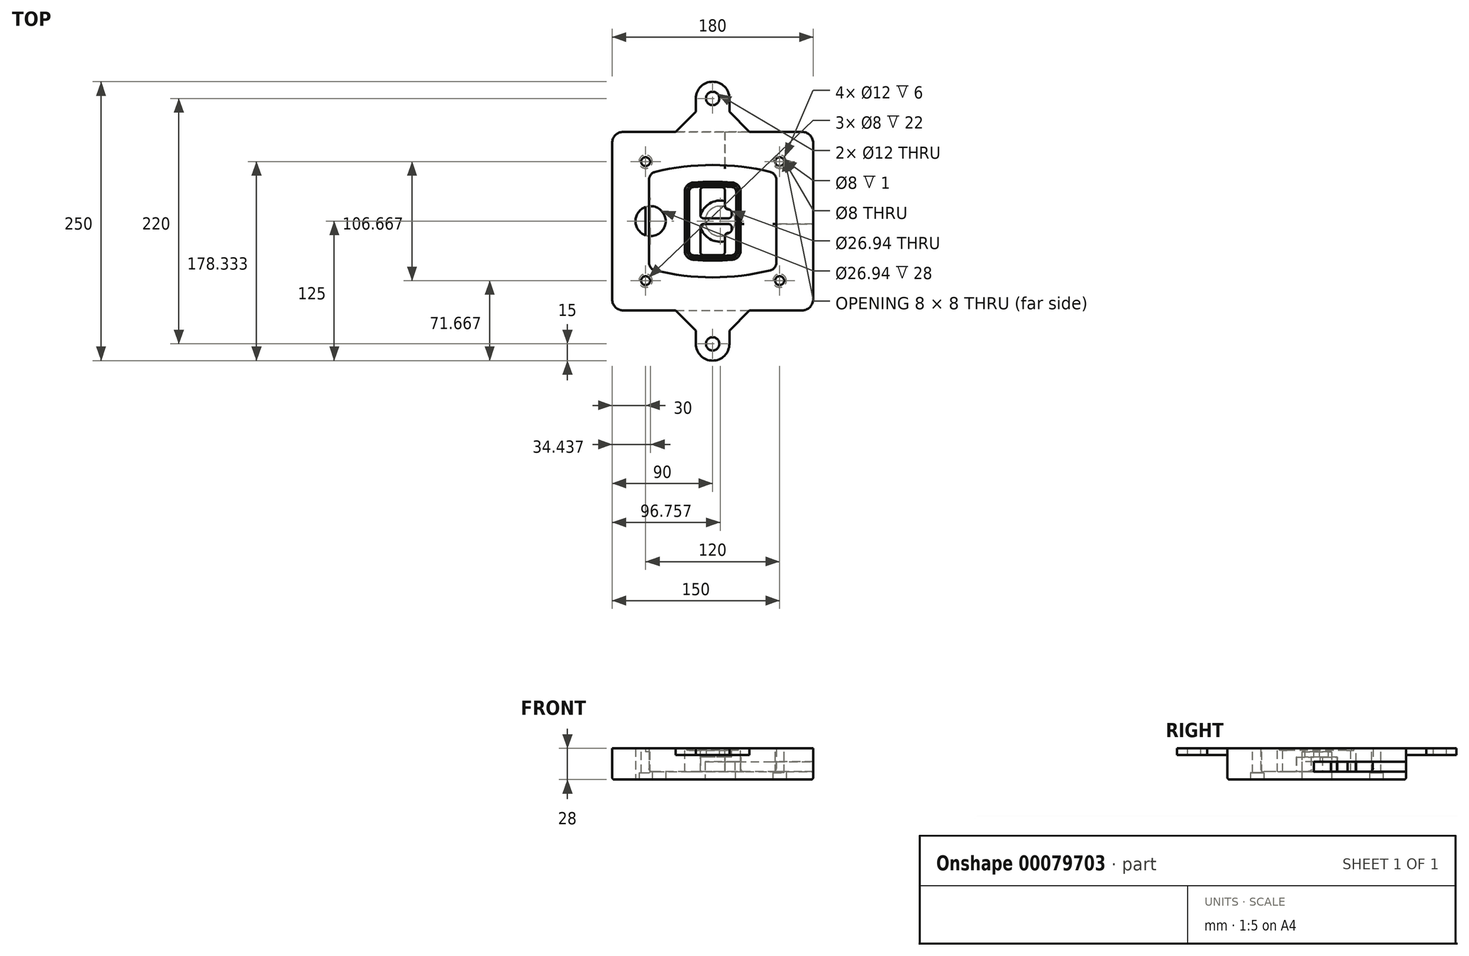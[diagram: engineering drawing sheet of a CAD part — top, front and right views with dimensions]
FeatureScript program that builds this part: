
annotation { "Feature Type Name" : "Feature", "Feature Type Description" : "" }
export const myFeature = defineFeature(function(context is Context, id is Id, definition is map)
    precondition{}
    {
        {
            var Q0;
            Q0=qCreatedBy(makeId("Top.planeOp"),FACE);
            var sketch = newSketch(context, id + "F0", { "sketchPlane" : qUnion([Q0])});
            skPoint(sketch, "E0.rect.middle", {"position": v(0, 0) * mm});
            skLineSegment(sketch, "E1.bottom", {"start": v(-80, -80) * mm, "end": v(80, -80) * mm});
            skLineSegment(sketch, "E1.top", {"start": v(-80, 80) * mm, "end": v(80, 80) * mm});
            skLineSegment(sketch, "E1.left", {"start": v(-90, -70) * mm, "end": v(-90, 70) * mm});
            skLineSegment(sketch, "E1.right", {"start": v(90, -70) * mm, "end": v(90, 70) * mm});
            skLineSegment(sketch, "E2", {"start": v(-90, 80) * mm, "end": v(90, -80) * mm, "construction": true});
            skLineSegment(sketch, "E3", {"start": v(90, 80) * mm, "end": v(-90, -80) * mm, "construction": true});
            skCircle(sketch, "E4", {"center": v(-60, 53.33) * mm, "radius": 4 * mm});
            skCircle(sketch, "E5", {"center": v(60, 53.33) * mm, "radius": 4 * mm});
            skCircle(sketch, "E6", {"center": v(60, -53.33) * mm, "radius": 4 * mm});
            skCircle(sketch, "E7", {"center": v(-60, -53.33) * mm, "radius": 4 * mm});
            skLineSegment(sketch, "E8", {"start": v(-60, 53.33) * mm, "end": v(60, 53.33) * mm, "construction": true});
            skLineSegment(sketch, "E9", {"start": v(60, 53.33) * mm, "end": v(60, -53.33) * mm, "construction": true});
            skLineSegment(sketch, "E10", {"start": v(60, -53.33) * mm, "end": v(-60, -53.33) * mm, "construction": true});
            skLineSegment(sketch, "E11", {"start": v(-60, -53.33) * mm, "end": v(-60, 53.33) * mm, "construction": true});
            skLineSegment(sketch, "E12", {"start": v(-60, 37.3) * mm, "end": v(-60, -37.3) * mm});
            skLineSegment(sketch, "E13", {"start": v(60, 37.3) * mm, "end": v(60, -37.3) * mm});
            skArc(sketch, "E14", {"start": v(52.38, 47.01) * mm, "mid": v(0, 53.33) * mm, "end": v(-52.38, 47.01) * mm});
            skArc(sketch, "E15", {"start": v(-52.38, -47.01) * mm, "mid": v(0, -53.33) * mm, "end": v(52.38, -47.01) * mm});
            skLineSegment(sketch, "E16", {"start": v(-60, 0) * mm, "end": v(60, 0) * mm, "construction": true});
            skPoint(sketch, "E17.visualSharp", {"position": v(-60, -45) * mm});
            skArc(sketch, "E17.filletArc", {"start": v(-60, -37.3) * mm, "mid": v(-57.87, -43.47) * mm, "end": v(-52.38, -47.01) * mm});
            skPoint(sketch, "E18.visualSharp", {"position": v(-60, 45) * mm});
            skArc(sketch, "E18.filletArc", {"start": v(-52.38, 47.01) * mm, "mid": v(-57.87, 43.47) * mm, "end": v(-60, 37.3) * mm});
            skPoint(sketch, "E19.visualSharp", {"position": v(60, 45) * mm});
            skArc(sketch, "E19.filletArc", {"start": v(60, 37.3) * mm, "mid": v(57.87, 43.47) * mm, "end": v(52.38, 47.01) * mm});
            skPoint(sketch, "E20.visualSharp", {"position": v(60, -45) * mm});
            skArc(sketch, "E20.filletArc", {"start": v(52.38, -47.01) * mm, "mid": v(57.87, -43.47) * mm, "end": v(60, -37.3) * mm});
            skPoint(sketch, "E21.visualSharp", {"position": v(-90, 80) * mm});
            skArc(sketch, "E21.filletArc", {"start": v(-80, 80) * mm, "mid": v(-87.07, 77.07) * mm, "end": v(-90, 70) * mm});
            skPoint(sketch, "E22.visualSharp", {"position": v(90, 80) * mm});
            skArc(sketch, "E22.filletArc", {"start": v(90, 70) * mm, "mid": v(87.07, 77.07) * mm, "end": v(80, 80) * mm});
            skPoint(sketch, "E23.visualSharp", {"position": v(90, -80) * mm});
            skArc(sketch, "E23.filletArc", {"start": v(80, -80) * mm, "mid": v(87.07, -77.07) * mm, "end": v(90, -70) * mm});
            skPoint(sketch, "E24.visualSharp", {"position": v(-90, -80) * mm});
            skArc(sketch, "E24.filletArc", {"start": v(-90, -70) * mm, "mid": v(-87.07, -77.07) * mm, "end": v(-80, -80) * mm});
            skArc(sketch, "E25.0", {"start": v(57, 37.3) * mm, "mid": v(55.5, 41.62) * mm, "end": v(51.67, 44.1) * mm});
            skLineSegment(sketch, "E25.1", {"start": v(57, 37.3) * mm, "end": v(57, -37.3) * mm});
            skArc(sketch, "E25.2", {"start": v(51.67, -44.1) * mm, "mid": v(55.5, -41.62) * mm, "end": v(57, -37.3) * mm});
            skArc(sketch, "E25.3", {"start": v(-51.67, -44.1) * mm, "mid": v(0, -50.33) * mm, "end": v(51.67, -44.1) * mm});
            skArc(sketch, "E25.4", {"start": v(-57, -37.3) * mm, "mid": v(-55.5, -41.62) * mm, "end": v(-51.67, -44.1) * mm});
            skArc(sketch, "E25.5", {"start": v(51.67, 44.1) * mm, "mid": v(0, 50.33) * mm, "end": v(-51.67, 44.1) * mm});
            skLineSegment(sketch, "E25.6", {"start": v(-57, 37.3) * mm, "end": v(-57, -37.3) * mm});
            skArc(sketch, "E25.7", {"start": v(-51.67, 44.1) * mm, "mid": v(-55.5, 41.62) * mm, "end": v(-57, 37.3) * mm});
            skArc(sketch, "E26.0", {"start": v(-53.33, 50.9) * mm, "mid": v(-61.01, 45.94) * mm, "end": v(-64, 37.3) * mm});
            skArc(sketch, "E26.1", {"start": v(53.33, 50.9) * mm, "mid": v(0, 57.33) * mm, "end": v(-53.33, 50.9) * mm});
            skArc(sketch, "E26.2", {"start": v(64, 37.3) * mm, "mid": v(61.01, 45.94) * mm, "end": v(53.33, 50.9) * mm});
            skLineSegment(sketch, "E26.3", {"start": v(64, 37.3) * mm, "end": v(64, -37.3) * mm});
            skArc(sketch, "E26.4", {"start": v(53.33, -50.9) * mm, "mid": v(61.01, -45.94) * mm, "end": v(64, -37.3) * mm});
            skLineSegment(sketch, "E26.5", {"start": v(-64, 37.3) * mm, "end": v(-64, -37.3) * mm});
            skArc(sketch, "E26.6", {"start": v(-53.33, -50.9) * mm, "mid": v(0, -57.33) * mm, "end": v(53.33, -50.9) * mm});
            skArc(sketch, "E26.7", {"start": v(-64, -37.3) * mm, "mid": v(-61.01, -45.94) * mm, "end": v(-53.33, -50.9) * mm});
            skSolve(sketch);
        }
        {
            var Q0;
            Q0=makeQuery(id+"F0.imprint","IMPRINT",FACE,{"disambiguationData":[TD([[makeQuery(id+"F0.imprint","IMPRINT",EDGE,{"derivedFrom":sQuery(id+"F0.wireOp",EDGE,"E1.bottom")}),1.0]])]});
            var Q1;
            Q1=makeQuery(id+"F0.imprint","IMPRINT",FACE,{"disambiguationData":[TD([[makeQuery(id+"F0.imprint","IMPRINT",EDGE,{"derivedFrom":sQuery(id+"F0.wireOp",EDGE,"E12")}),1.0]])]});
            var Q2;
            Q2=makeQuery(id+"F0.imprint","IMPRINT",FACE,{"disambiguationData":[TD([[makeQuery(id+"F0.imprint","IMPRINT",EDGE,{"derivedFrom":sQuery(id+"F0.wireOp",EDGE,"E25.0")}),1.0]])]});
            var Q3;
            Q3=makeQuery(id+"F0.imprint","IMPRINT",FACE,{"disambiguationData":[TD([[makeQuery(id+"F0.imprint","IMPRINT",EDGE,{"derivedFrom":sQuery(id+"F0.wireOp",EDGE,"E12")}),-1.0]])]});
            extrude(context, id + "F1", {"entities" : qUnion([Q0, Q1, Q2, Q3]), "oppositeDirection" : true, "depth" : 25 * mm});
        }
        {
            var Q0;
            Q0=makeQuery(id+"F0.imprint","IMPRINT",FACE,{"disambiguationData":[TD([[makeQuery(id+"F0.imprint","IMPRINT",EDGE,{"derivedFrom":sQuery(id+"F0.wireOp",EDGE,"E12")}),1.0]])]});
            extrude(context, id + "F2", {"entities" : qUnion([Q0]), "operationType" : NewBodyOperationType.ADD, "depth" : 3 * mm});
        }
        {
            var Q0;
            Q0=makeQuery(id+"F0.imprint","IMPRINT",FACE,{"disambiguationData":[TD([[makeQuery(id+"F0.imprint","IMPRINT",EDGE,{"derivedFrom":sQuery(id+"F0.wireOp",EDGE,"E25.0")}),1.0]])]});
            extrude(context, id + "F3", {"entities" : qUnion([Q0]), "operationType" : NewBodyOperationType.REMOVE, "oppositeDirection" : true, "depth" : 18 * mm});
        }
        {
            var Q0;
            Q0=makeQuery(id+"F2.opExtrude","CAP_FACE",FACE,{"disambiguationData":[OSD([sQuery(id+"F0.wireOp",EDGE,"E12"),sQuery(id+"F0.wireOp",EDGE,"E13"),sQuery(id+"F0.wireOp",EDGE,"E14"),sQuery(id+"F0.wireOp",EDGE,"E15"),sQuery(id+"F0.wireOp",EDGE,"E17.filletArc"),sQuery(id+"F0.wireOp",EDGE,"E18.filletArc"),sQuery(id+"F0.wireOp",EDGE,"E19.filletArc"),sQuery(id+"F0.wireOp",EDGE,"E20.filletArc"),sQuery(id+"F0.wireOp",EDGE,"E25.0"),sQuery(id+"F0.wireOp",EDGE,"E25.1"),sQuery(id+"F0.wireOp",EDGE,"E25.2"),sQuery(id+"F0.wireOp",EDGE,"E25.3"),sQuery(id+"F0.wireOp",EDGE,"E25.4"),sQuery(id+"F0.wireOp",EDGE,"E25.5"),sQuery(id+"F0.wireOp",EDGE,"E25.6"),sQuery(id+"F0.wireOp",EDGE,"E25.7")])],"isStart":false});
            var sketch = newSketch(context, id + "F4", { "sketchPlane" : qUnion([Q0])});
            skArc(sketch, "E27.0", {"start": v(-17.7, -34.56) * mm, "mid": v(0, -35.33) * mm, "end": v(17.7, -34.56) * mm});
            skArc(sketch, "E28.0", {"start": v(17.7, 34.56) * mm, "mid": v(0, 35.33) * mm, "end": v(-17.7, 34.56) * mm});
            skLineSegment(sketch, "E29", {"start": v(-25, 26.59) * mm, "end": v(-25, -26.59) * mm});
            skLineSegment(sketch, "E30", {"start": v(25, 26.59) * mm, "end": v(25, -26.59) * mm});
            skLineSegment(sketch, "E31", {"start": v(-25, 33.78) * mm, "end": v(25, 33.78) * mm, "construction": true});
            skLineSegment(sketch, "E32", {"start": v(-25, -33.78) * mm, "end": v(25, -33.78) * mm, "construction": true});
            skPoint(sketch, "E33.visualSharp", {"position": v(-25, 33.78) * mm});
            skArc(sketch, "E33.filletArc", {"start": v(-17.7, 34.56) * mm, "mid": v(-22.9, 32) * mm, "end": v(-25, 26.59) * mm});
            skPoint(sketch, "E34.visualSharp", {"position": v(25, 33.78) * mm});
            skArc(sketch, "E34.filletArc", {"start": v(25, 26.59) * mm, "mid": v(22.9, 32) * mm, "end": v(17.7, 34.56) * mm});
            skPoint(sketch, "E35.visualSharp", {"position": v(25, -33.78) * mm});
            skArc(sketch, "E35.filletArc", {"start": v(17.7, -34.56) * mm, "mid": v(22.9, -32) * mm, "end": v(25, -26.59) * mm});
            skPoint(sketch, "E36.visualSharp", {"position": v(-25, -33.78) * mm});
            skArc(sketch, "E36.filletArc", {"start": v(-25, -26.59) * mm, "mid": v(-22.9, -32) * mm, "end": v(-17.7, -34.56) * mm});
            skArc(sketch, "E37.0", {"start": v(51.67, 44.1) * mm, "mid": v(0, 50.33) * mm, "end": v(-51.67, 44.1) * mm});
            skArc(sketch, "E37.1", {"start": v(-51.67, 44.1) * mm, "mid": v(-55.5, 41.62) * mm, "end": v(-57, 37.3) * mm});
            skLineSegment(sketch, "E37.2", {"start": v(-57, 37.3) * mm, "end": v(-57, -37.3) * mm});
            skArc(sketch, "E37.3", {"start": v(-57, -37.3) * mm, "mid": v(-55.5, -41.62) * mm, "end": v(-51.67, -44.1) * mm});
            skArc(sketch, "E37.4", {"start": v(-51.67, -44.1) * mm, "mid": v(0, -50.33) * mm, "end": v(51.67, -44.1) * mm});
            skArc(sketch, "E37.5", {"start": v(51.67, -44.1) * mm, "mid": v(55.5, -41.62) * mm, "end": v(57, -37.3) * mm});
            skLineSegment(sketch, "E37.6", {"start": v(57, 37.3) * mm, "end": v(57, -37.3) * mm});
            skArc(sketch, "E37.7", {"start": v(57, 37.3) * mm, "mid": v(55.5, 41.62) * mm, "end": v(51.67, 44.1) * mm});
            skLineSegment(sketch, "E38.0", {"start": v(23, 26.59) * mm, "end": v(23, -26.59) * mm});
            skArc(sketch, "E38.1", {"start": v(17.53, -32.56) * mm, "mid": v(21.42, -30.64) * mm, "end": v(23, -26.59) * mm});
            skArc(sketch, "E38.2", {"start": v(-17.53, -32.56) * mm, "mid": v(0, -33.33) * mm, "end": v(17.53, -32.56) * mm});
            skArc(sketch, "E38.3", {"start": v(-23, -26.59) * mm, "mid": v(-21.42, -30.64) * mm, "end": v(-17.53, -32.56) * mm});
            skLineSegment(sketch, "E38.4", {"start": v(-23, 26.59) * mm, "end": v(-23, -26.59) * mm});
            skArc(sketch, "E38.5", {"start": v(23, 26.59) * mm, "mid": v(21.42, 30.64) * mm, "end": v(17.53, 32.56) * mm});
            skArc(sketch, "E38.6", {"start": v(-17.53, 32.56) * mm, "mid": v(-21.42, 30.64) * mm, "end": v(-23, 26.59) * mm});
            skArc(sketch, "E38.7", {"start": v(17.53, 32.56) * mm, "mid": v(0, 33.33) * mm, "end": v(-17.53, 32.56) * mm});
            skArc(sketch, "E39.0", {"start": v(21, 26.59) * mm, "mid": v(19.95, 29.29) * mm, "end": v(17.35, 30.57) * mm});
            skLineSegment(sketch, "E39.1", {"start": v(21, 26.59) * mm, "end": v(21, -26.59) * mm});
            skArc(sketch, "E39.2", {"start": v(17.35, -30.57) * mm, "mid": v(19.95, -29.29) * mm, "end": v(21, -26.59) * mm});
            skArc(sketch, "E39.3", {"start": v(-17.35, -30.57) * mm, "mid": v(0, -31.33) * mm, "end": v(17.35, -30.57) * mm});
            skArc(sketch, "E39.4", {"start": v(-21, -26.59) * mm, "mid": v(-19.95, -29.29) * mm, "end": v(-17.35, -30.57) * mm});
            skArc(sketch, "E39.5", {"start": v(17.35, 30.57) * mm, "mid": v(0, 31.33) * mm, "end": v(-17.35, 30.57) * mm});
            skLineSegment(sketch, "E39.6", {"start": v(-21, 26.59) * mm, "end": v(-21, -26.59) * mm});
            skArc(sketch, "E39.7", {"start": v(-17.35, 30.57) * mm, "mid": v(-19.95, 29.29) * mm, "end": v(-21, 26.59) * mm});
            skLineSegment(sketch, "E40", {"start": v(-25, 0) * mm, "end": v(25, 0) * mm, "construction": true});
            skLineSegment(sketch, "E41", {"start": v(-11, 5.5) * mm, "end": v(-11, 27.5) * mm});
            skLineSegment(sketch, "E42", {"start": v(-8, 30.5) * mm, "end": v(8, 30.5) * mm});
            skLineSegment(sketch, "E43", {"start": v(11, 27.5) * mm, "end": v(11, 13.5) * mm});
            skLineSegment(sketch, "E44", {"start": v(14, 10.5) * mm, "end": v(14, 10.5) * mm});
            skLineSegment(sketch, "E45", {"start": v(17, 7.5) * mm, "end": v(17, 5.5) * mm});
            skLineSegment(sketch, "E46", {"start": v(14, 2.5) * mm, "end": v(-8, 2.5) * mm});
            skPoint(sketch, "E47.visualSharp", {"position": v(-11, 30.5) * mm});
            skArc(sketch, "E47.filletArc", {"start": v(-8, 30.5) * mm, "mid": v(-10.12, 29.62) * mm, "end": v(-11, 27.5) * mm});
            skPoint(sketch, "E48.visualSharp", {"position": v(11, 30.5) * mm});
            skArc(sketch, "E48.filletArc", {"start": v(11, 27.5) * mm, "mid": v(10.12, 29.62) * mm, "end": v(8, 30.5) * mm});
            skPoint(sketch, "E49.visualSharp", {"position": v(11, 10.5) * mm});
            skArc(sketch, "E49.filletArc", {"start": v(11, 13.5) * mm, "mid": v(11.88, 11.38) * mm, "end": v(14, 10.5) * mm});
            skPoint(sketch, "E50.visualSharp", {"position": v(17, 10.5) * mm});
            skArc(sketch, "E50.filletArc", {"start": v(17, 7.5) * mm, "mid": v(16.12, 9.62) * mm, "end": v(14, 10.5) * mm});
            skPoint(sketch, "E51.visualSharp", {"position": v(17, 2.5) * mm});
            skArc(sketch, "E51.filletArc", {"start": v(14, 2.5) * mm, "mid": v(16.12, 3.38) * mm, "end": v(17, 5.5) * mm});
            skPoint(sketch, "E52.visualSharp", {"position": v(-11, 2.5) * mm});
            skArc(sketch, "E52.filletArc", {"start": v(-11, 5.5) * mm, "mid": v(-10.12, 3.38) * mm, "end": v(-8, 2.5) * mm});
            skLineSegment(sketch, "E53.0.MirrorCS", {"start": v(14, -2.5) * mm, "end": v(-8, -2.5) * mm});
            skArc(sketch, "E54.0.MirrorCS", {"start": v(-11, -5.5) * mm, "mid": v(-10.12, -3.38) * mm, "end": v(-8, -2.5) * mm});
            skLineSegment(sketch, "E55.0.MirrorCS", {"start": v(-11, -5.5) * mm, "end": v(-11, -27.5) * mm});
            skArc(sketch, "E56.0.MirrorCS", {"start": v(-8, -30.5) * mm, "mid": v(-10.12, -29.62) * mm, "end": v(-11, -27.5) * mm});
            skLineSegment(sketch, "E57.0.MirrorCS", {"start": v(-8, -30.5) * mm, "end": v(8, -30.5) * mm});
            skArc(sketch, "E58.0.MirrorCS", {"start": v(11, -27.5) * mm, "mid": v(10.12, -29.62) * mm, "end": v(8, -30.5) * mm});
            skLineSegment(sketch, "E59.0.MirrorCS", {"start": v(11, -27.5) * mm, "end": v(11, -13.5) * mm});
            skArc(sketch, "E60.0.MirrorCS", {"start": v(11, -13.5) * mm, "mid": v(11.88, -11.38) * mm, "end": v(14, -10.5) * mm});
            skArc(sketch, "E61.0.MirrorCS", {"start": v(17, -7.5) * mm, "mid": v(16.12, -9.62) * mm, "end": v(14, -10.5) * mm});
            skLineSegment(sketch, "E62.0.MirrorCS", {"start": v(17, -7.5) * mm, "end": v(17, -5.5) * mm});
            skArc(sketch, "E63.0.MirrorCS", {"start": v(14, -2.5) * mm, "mid": v(16.12, -3.38) * mm, "end": v(17, -5.5) * mm});
            skSolve(sketch);
        }
        {
            var Q0;
            Q0=makeQuery(id+"F4.imprint","IMPRINT",FACE,{"disambiguationData":[TD([[makeQuery(id+"F4.imprint","IMPRINT",EDGE,{"derivedFrom":sQuery(id+"F4.wireOp",EDGE,"E27.0")}),1.0]])]});
            var Q1;
            Q1=makeQuery(id+"F4.imprint","IMPRINT",FACE,{"disambiguationData":[TD([[makeQuery(id+"F4.imprint","IMPRINT",EDGE,{"derivedFrom":sQuery(id+"F4.wireOp",EDGE,"E38.0")}),-1.0]])]});
            var Q2;
            Q2=makeQuery(id+"F4.imprint","IMPRINT",FACE,{"disambiguationData":[TD([[makeQuery(id+"F4.imprint","IMPRINT",EDGE,{"derivedFrom":sQuery(id+"F4.wireOp",EDGE,"E39.0")}),1.0]])]});
            extrude(context, id + "F5", {"entities" : qUnion([Q0, Q1, Q2]), "operationType" : NewBodyOperationType.ADD, "endBound" : BoundingType.UP_TO_NEXT, "oppositeDirection" : true, "depth" : 25 * mm});
        }
        {
            var Q0;
            Q0=makeQuery(id+"F4.imprint","IMPRINT",FACE,{"disambiguationData":[TD([[makeQuery(id+"F4.imprint","IMPRINT",EDGE,{"derivedFrom":sQuery(id+"F4.wireOp",EDGE,"E38.0")}),-1.0]])]});
            extrude(context, id + "F6", {"entities" : qUnion([Q0]), "operationType" : NewBodyOperationType.REMOVE, "oppositeDirection" : true, "depth" : 2 * mm});
        }
        {
            var Q0;
            Q0=makeQuery(id+"F1.opExtrude","CAP_FACE",FACE,{"disambiguationData":[OSD([sQuery(id+"F0.wireOp",EDGE,"E1.bottom"),sQuery(id+"F0.wireOp",EDGE,"E1.top"),sQuery(id+"F0.wireOp",EDGE,"E1.left"),sQuery(id+"F0.wireOp",EDGE,"E1.right"),sQuery(id+"F0.wireOp",EDGE,"E4"),sQuery(id+"F0.wireOp",EDGE,"E5"),sQuery(id+"F0.wireOp",EDGE,"E6"),sQuery(id+"F0.wireOp",EDGE,"E7"),sQuery(id+"F0.wireOp",EDGE,"E21.filletArc"),sQuery(id+"F0.wireOp",EDGE,"E22.filletArc"),sQuery(id+"F0.wireOp",EDGE,"E23.filletArc"),sQuery(id+"F0.wireOp",EDGE,"E24.filletArc")])],"isStart":false});
            var sketch = newSketch(context, id + "F7", { "sketchPlane" : qUnion([Q0])});
            skCircle(sketch, "E64", {"center": v(6.76, 0) * mm, "radius": 13.47 * mm});
            skCircle(sketch, "E65", {"center": v(-55.56, 0) * mm, "radius": 13.47 * mm});
            skLineSegment(sketch, "E66", {"start": v(90, 0) * mm, "end": v(-90, 0) * mm});
            skCircle(sketch, "E67", {"center": v(6.76, 0) * mm, "radius": 18.47 * mm});
            skCircle(sketch, "E68", {"center": v(60, -53.33) * mm, "radius": 6 * mm});
            skCircle(sketch, "E69", {"center": v(-60, -53.33) * mm, "radius": 6 * mm});
            skCircle(sketch, "E70", {"center": v(-60, 53.33) * mm, "radius": 6 * mm});
            skCircle(sketch, "E71", {"center": v(60, 53.33) * mm, "radius": 6 * mm});
            skSolve(sketch);
        }
        {
            var Q0;
            {var subQ1=sQuery(id+"F7.wireOp",EDGE,"E66");var subQ4=sQuery(id+"F7.wireOp",EDGE,"E64");var subQ6=makeQuery(id+"F7.imprint","INTERSECT",VERTEX,{"disambiguationData":[OD(0.0)],"derivedFrom":[subQ4,subQ1]});Q0=makeQuery(id+"F7.imprint","IMPRINT",FACE,{"disambiguationData":[TD([[makeQuery(id+"F7.imprint","IMPRINT",EDGE,{"disambiguationData":[TD([[subQ6,-1.0]])],"derivedFrom":subQ4}),-1.0]])]});}
            var Q1;
            {var subQ0=sQuery(id+"F7.wireOp",EDGE,"E66");var subQ1=sQuery(id+"F7.wireOp",EDGE,"E64");var subQ3=makeQuery(id+"F7.imprint","INTERSECT",VERTEX,{"disambiguationData":[OD(0.0)],"derivedFrom":[subQ1,subQ0]});Q1=makeQuery(id+"F7.imprint","IMPRINT",FACE,{"disambiguationData":[TD([[makeQuery(id+"F7.imprint","IMPRINT",EDGE,{"disambiguationData":[TD([[subQ3,-1.0]])],"derivedFrom":subQ1}),1.0]])]});}
            var Q2;
            {var subQ0=sQuery(id+"F7.wireOp",EDGE,"E66");var subQ1=sQuery(id+"F7.wireOp",EDGE,"E64");var subQ3=makeQuery(id+"F7.imprint","INTERSECT",VERTEX,{"disambiguationData":[OD(0.0)],"derivedFrom":[subQ1,subQ0]});Q2=makeQuery(id+"F7.imprint","IMPRINT",FACE,{"disambiguationData":[TD([[makeQuery(id+"F7.imprint","IMPRINT",EDGE,{"disambiguationData":[TD([[subQ3,1.0]])],"derivedFrom":subQ1}),1.0]])]});}
            var Q3;
            {var subQ1=sQuery(id+"F7.wireOp",EDGE,"E66");var subQ4=sQuery(id+"F7.wireOp",EDGE,"E64");var subQ6=makeQuery(id+"F7.imprint","INTERSECT",VERTEX,{"disambiguationData":[OD(0.0)],"derivedFrom":[subQ4,subQ1]});Q3=makeQuery(id+"F7.imprint","IMPRINT",FACE,{"disambiguationData":[TD([[makeQuery(id+"F7.imprint","IMPRINT",EDGE,{"disambiguationData":[TD([[subQ6,1.0]])],"derivedFrom":subQ4}),-1.0]])]});}
            extrude(context, id + "F8", {"entities" : qUnion([Q0, Q1, Q2, Q3]), "operationType" : NewBodyOperationType.ADD, "oppositeDirection" : true, "depth" : 20 * mm});
        }
        {
            var Q0;
            {var subQ0=sQuery(id+"F7.wireOp",EDGE,"E66");var subQ1=sQuery(id+"F7.wireOp",EDGE,"E64");var subQ3=makeQuery(id+"F7.imprint","INTERSECT",VERTEX,{"disambiguationData":[OD(0.0)],"derivedFrom":[subQ1,subQ0]});Q0=makeQuery(id+"F7.imprint","IMPRINT",FACE,{"disambiguationData":[TD([[makeQuery(id+"F7.imprint","IMPRINT",EDGE,{"disambiguationData":[TD([[subQ3,-1.0]])],"derivedFrom":subQ1}),1.0]])]});}
            var Q1;
            {var subQ0=sQuery(id+"F7.wireOp",EDGE,"E66");var subQ1=sQuery(id+"F7.wireOp",EDGE,"E64");var subQ3=makeQuery(id+"F7.imprint","INTERSECT",VERTEX,{"disambiguationData":[OD(0.0)],"derivedFrom":[subQ1,subQ0]});Q1=makeQuery(id+"F7.imprint","IMPRINT",FACE,{"disambiguationData":[TD([[makeQuery(id+"F7.imprint","IMPRINT",EDGE,{"disambiguationData":[TD([[subQ3,1.0]])],"derivedFrom":subQ1}),1.0]])]});}
            extrude(context, id + "F9", {"entities" : qUnion([Q0, Q1]), "operationType" : NewBodyOperationType.REMOVE, "oppositeDirection" : true, "depth" : 16 * mm});
        }
        {
            var Q0;
            {var subQ0=sQuery(id+"F7.wireOp",EDGE,"E66");var subQ1=sQuery(id+"F7.wireOp",EDGE,"E65");var subQ3=makeQuery(id+"F7.imprint","INTERSECT",VERTEX,{"disambiguationData":[OD(0.0)],"derivedFrom":[subQ1,subQ0]});Q0=makeQuery(id+"F7.imprint","IMPRINT",FACE,{"disambiguationData":[TD([[makeQuery(id+"F7.imprint","IMPRINT",EDGE,{"disambiguationData":[TD([[subQ3,-1.0]])],"derivedFrom":subQ1}),1.0]])]});}
            var Q1;
            {var subQ0=sQuery(id+"F7.wireOp",EDGE,"E66");var subQ1=sQuery(id+"F7.wireOp",EDGE,"E65");var subQ3=makeQuery(id+"F7.imprint","INTERSECT",VERTEX,{"disambiguationData":[OD(0.0)],"derivedFrom":[subQ1,subQ0]});Q1=makeQuery(id+"F7.imprint","IMPRINT",FACE,{"disambiguationData":[TD([[makeQuery(id+"F7.imprint","IMPRINT",EDGE,{"disambiguationData":[TD([[subQ3,1.0]])],"derivedFrom":subQ1}),1.0]])]});}
            extrude(context, id + "F10", {"entities" : qUnion([Q0, Q1]), "operationType" : NewBodyOperationType.REMOVE, "oppositeDirection" : true, "depth" : 25 * mm});
        }
        {
            var Q0;
            Q0=makeQuery(id+"F7.imprint","IMPRINT",FACE,{"disambiguationData":[TD([[makeQuery(id+"F7.imprint","IMPRINT",EDGE,{"derivedFrom":sQuery(id+"F7.wireOp",EDGE,"E68")}),1.0]])]});
            var Q1;
            Q1=makeQuery(id+"F7.imprint","IMPRINT",FACE,{"disambiguationData":[TD([[makeQuery(id+"F7.imprint","IMPRINT",EDGE,{"derivedFrom":makeQuery(id+"F1.opExtrude","CAP_EDGE",EDGE,{"disambiguationData":[OSD([sQuery(id+"F0.wireOp",EDGE,"E5")])],"isStart":false})}),-1.0]])]});
            var Q2;
            Q2=makeQuery(id+"F7.imprint","IMPRINT",FACE,{"disambiguationData":[TD([[makeQuery(id+"F7.imprint","IMPRINT",EDGE,{"derivedFrom":sQuery(id+"F7.wireOp",EDGE,"E69")}),1.0]])]});
            var Q3;
            Q3=makeQuery(id+"F7.imprint","IMPRINT",FACE,{"disambiguationData":[TD([[makeQuery(id+"F7.imprint","IMPRINT",EDGE,{"derivedFrom":makeQuery(id+"F1.opExtrude","CAP_EDGE",EDGE,{"disambiguationData":[OSD([sQuery(id+"F0.wireOp",EDGE,"E4")])],"isStart":false})}),-1.0]])]});
            var Q4;
            Q4=makeQuery(id+"F7.imprint","IMPRINT",FACE,{"disambiguationData":[TD([[makeQuery(id+"F7.imprint","IMPRINT",EDGE,{"derivedFrom":sQuery(id+"F7.wireOp",EDGE,"E70")}),1.0]])]});
            var Q5;
            Q5=makeQuery(id+"F7.imprint","IMPRINT",FACE,{"disambiguationData":[TD([[makeQuery(id+"F7.imprint","IMPRINT",EDGE,{"derivedFrom":makeQuery(id+"F1.opExtrude","CAP_EDGE",EDGE,{"disambiguationData":[OSD([sQuery(id+"F0.wireOp",EDGE,"E7")])],"isStart":false})}),-1.0]])]});
            var Q6;
            Q6=makeQuery(id+"F7.imprint","IMPRINT",FACE,{"disambiguationData":[TD([[makeQuery(id+"F7.imprint","IMPRINT",EDGE,{"derivedFrom":sQuery(id+"F7.wireOp",EDGE,"E71")}),1.0]])]});
            var Q7;
            Q7=makeQuery(id+"F7.imprint","IMPRINT",FACE,{"disambiguationData":[TD([[makeQuery(id+"F7.imprint","IMPRINT",EDGE,{"derivedFrom":makeQuery(id+"F1.opExtrude","CAP_EDGE",EDGE,{"disambiguationData":[OSD([sQuery(id+"F0.wireOp",EDGE,"E6")])],"isStart":false})}),-1.0]])]});
            extrude(context, id + "F11", {"entities" : qUnion([Q0, Q1, Q2, Q3, Q4, Q5, Q6, Q7]), "operationType" : NewBodyOperationType.REMOVE, "oppositeDirection" : true, "depth" : 6 * mm});
        }
        {
            var Q0;
            Q0=makeQuery(id+"F9.boolean.opBoolean","COPY",FACE,{"derivedFrom":makeQuery(id+"F9.opExtrude","CAP_FACE",FACE,{"disambiguationData":[OSD([sQuery(id+"F7.wireOp",EDGE,"E64")])],"isStart":false})});
            var sketch = newSketch(context, id + "F12", { "sketchPlane" : qUnion([Q0])});
            skArc(sketch, "E72.0", {"start": v(11, -88.19) * mm, "mid": v(97.1, -83.6) * mm, "end": v(92.5, 2.5) * mm});
            skLineSegment(sketch, "E72.1", {"start": v(11, -17.97) * mm, "end": v(11, -17.97) * mm});
            skLineSegment(sketch, "E73", {"start": v(92.5, -105.13) * mm, "end": v(102.3, -105.13) * mm});
            skLineSegment(sketch, "E74.0", {"start": v(92.5, 2.5) * mm, "end": v(14, 2.5) * mm});
            skArc(sketch, "E74.1", {"start": v(14, 2.5) * mm, "mid": v(16.12, 3.38) * mm, "end": v(17, 5.5) * mm});
            skLineSegment(sketch, "E74.2", {"start": v(17, 7.5) * mm, "end": v(17, 5.5) * mm});
            skArc(sketch, "E74.3", {"start": v(17, 7.5) * mm, "mid": v(16.12, 9.62) * mm, "end": v(14, 10.5) * mm});
            skArc(sketch, "E74.4", {"start": v(11, 13.5) * mm, "mid": v(11.88, 11.38) * mm, "end": v(14, 10.5) * mm});
            skLineSegment(sketch, "E74.5", {"start": v(11, 13.5) * mm, "end": v(11, -88.19) * mm});
            skLineSegment(sketch, "E74.7", {"start": v(92.5, -2.5) * mm, "end": v(14, -2.5) * mm});
            skArc(sketch, "E74.8", {"start": v(14, -2.5) * mm, "mid": v(16.12, -3.38) * mm, "end": v(17, -5.5) * mm});
            skLineSegment(sketch, "E74.9", {"start": v(17, -7.5) * mm, "end": v(17, -5.5) * mm});
            skArc(sketch, "E74.10", {"start": v(17, -7.5) * mm, "mid": v(16.12, -9.62) * mm, "end": v(14, -10.5) * mm});
            skArc(sketch, "E74.11", {"start": v(11, -13.5) * mm, "mid": v(11.88, -11.38) * mm, "end": v(14, -10.5) * mm});
            skLineSegment(sketch, "E74.12", {"start": v(11, -17.97) * mm, "end": v(11, -13.5) * mm});
            skPoint(sketch, "E75.orphan", {"position": v(11, -27.5) * mm});
            skPoint(sketch, "E76.orphan", {"position": v(-8, -2.5) * mm});
            skPoint(sketch, "E77.orphan", {"position": v(-8, 2.5) * mm});
            skPoint(sketch, "E78.orphan", {"position": v(11, 27.5) * mm});
            skSolve(sketch);
        }
        {
            var Q0;
            {var subQ7=sQuery(id+"F12.wireOp",EDGE,"E72.0");var subQ14=sQuery(id+"F12.wireOp",EDGE,"E72.1");var subQ16=sQuery(id+"F12.wireOp",EDGE,"E74.1");var subQ18=sQuery(id+"F12.wireOp",EDGE,"E74.8");Q0=qUnion([makeQuery(id+"F12.imprint","IMPRINT",FACE,{"disambiguationData":[TD([[makeQuery(id+"F12.imprint","IMPRINT",EDGE,{"derivedFrom":subQ7}),1.0]])]}),makeQuery(id+"F12.imprint","IMPRINT",FACE,{"disambiguationData":[TD([[makeQuery(id+"F12.imprint","IMPRINT",EDGE,{"derivedFrom":subQ14}),1.0]])]}),makeQuery(id+"F12.imprint","IMPRINT",FACE,{"disambiguationData":[TD([[makeQuery(id+"F12.imprint","IMPRINT",EDGE,{"derivedFrom":subQ16}),1.0]])]}),makeQuery(id+"F12.imprint","IMPRINT",FACE,{"disambiguationData":[TD([[makeQuery(id+"F12.imprint","IMPRINT",EDGE,{"derivedFrom":subQ18}),-1.0]])]})]);}
            var Q1;
            Q1=makeQuery(id+"F5.boolean.opBoolean","SPLIT",FACE,{"disambiguationData":[TD([makeQuery(id+"F5.opExtrude","SWEPT_FACE",FACE,{"disambiguationData":[OSD([sQuery(id+"F4.wireOp",EDGE,"E41")])]})])],"derivedFrom":makeQuery(id+"F3.boolean.opBoolean","COPY",FACE,{"derivedFrom":makeQuery(id+"F3.opExtrude","CAP_FACE",FACE,{"disambiguationData":[OSD([sQuery(id+"F0.wireOp",EDGE,"E25.0"),sQuery(id+"F0.wireOp",EDGE,"E25.1"),sQuery(id+"F0.wireOp",EDGE,"E25.2"),sQuery(id+"F0.wireOp",EDGE,"E25.3"),sQuery(id+"F0.wireOp",EDGE,"E25.4"),sQuery(id+"F0.wireOp",EDGE,"E25.5"),sQuery(id+"F0.wireOp",EDGE,"E25.6"),sQuery(id+"F0.wireOp",EDGE,"E25.7")])],"isStart":false})})});
            extrude(context, id + "F13", {"entities" : qUnion([Q0]), "operationType" : NewBodyOperationType.REMOVE, "endBound" : BoundingType.UP_TO_SURFACE, "endBoundEntityFace" : qUnion([Q1]), "depth" : 25 * mm});
        }
        {
            var Q0;
            Q0=makeQuery(id+"F3.boolean.opBoolean","COPY",EDGE,{"derivedFrom":makeQuery(id+"F3.opExtrude","CAP_EDGE",EDGE,{"disambiguationData":[OSD([sQuery(id+"F0.wireOp",EDGE,"E25.6")])],"isStart":false})});
            var Q1;
            Q1=makeQuery(id+"F8.boolean.opBoolean","INTERSECT",EDGE,{"derivedFrom":[makeQuery(id+"F5.opExtrude","SWEPT_FACE",FACE,{"disambiguationData":[OSD([sQuery(id+"F4.wireOp",EDGE,"E30")])]}),makeQuery(id+"F8.opExtrude","CAP_FACE",FACE,{"disambiguationData":[OSD([sQuery(id+"F7.wireOp",EDGE,"E67")])],"isStart":false})]});
            var Q2;
            Q2=makeQuery(id+"F8.boolean.opBoolean","INTERSECT",EDGE,{"disambiguationData":[OD(1.0)],"derivedFrom":[makeQuery(id+"F5.opExtrude","SWEPT_FACE",FACE,{"disambiguationData":[OSD([sQuery(id+"F4.wireOp",EDGE,"E30")])]}),makeQuery(id+"F8.opExtrude","SWEPT_FACE",FACE,{"disambiguationData":[OSD([sQuery(id+"F7.wireOp",EDGE,"E67")])]})]});
            var Q3;
            {var subQ0=makeQuery(id+"F3.boolean.opBoolean","COPY",FACE,{"derivedFrom":makeQuery(id+"F3.opExtrude","CAP_FACE",FACE,{"disambiguationData":[OSD([sQuery(id+"F0.wireOp",EDGE,"E25.0"),sQuery(id+"F0.wireOp",EDGE,"E25.1"),sQuery(id+"F0.wireOp",EDGE,"E25.2"),sQuery(id+"F0.wireOp",EDGE,"E25.3"),sQuery(id+"F0.wireOp",EDGE,"E25.4"),sQuery(id+"F0.wireOp",EDGE,"E25.5"),sQuery(id+"F0.wireOp",EDGE,"E25.6"),sQuery(id+"F0.wireOp",EDGE,"E25.7")])],"isStart":false})});var subQ1=sQuery(id+"F4.wireOp",EDGE,"E30");Q3=makeQuery(id+"F8.boolean.opBoolean","SPLIT",EDGE,{"disambiguationData":[TD([makeQuery(id+"F5.opExtrude","SWEPT_FACE",FACE,{"disambiguationData":[OSD([sQuery(id+"F4.wireOp",EDGE,"E35.filletArc")])]})])],"derivedFrom":makeQuery(id+"F5.opExtrude","TWEAK_EDGE",EDGE,{"derivedFrom":[subQ0,makeQuery(id+"F4.imprint","IMPRINT",EDGE,{"derivedFrom":subQ1})]})});}
            var Q4;
            {var subQ0=sQuery(id+"F0.wireOp",EDGE,"E25.0");var subQ1=sQuery(id+"F0.wireOp",EDGE,"E25.1");var subQ2=sQuery(id+"F0.wireOp",EDGE,"E25.2");var subQ3=sQuery(id+"F0.wireOp",EDGE,"E25.3");var subQ4=sQuery(id+"F0.wireOp",EDGE,"E25.4");var subQ5=sQuery(id+"F0.wireOp",EDGE,"E25.5");var subQ6=sQuery(id+"F0.wireOp",EDGE,"E25.6");var subQ7=sQuery(id+"F0.wireOp",EDGE,"E25.7");Q4=makeQuery(id+"F8.boolean.opBoolean","INTERSECT",EDGE,{"derivedFrom":[makeQuery(id+"F5.boolean.opBoolean","SPLIT",FACE,{"disambiguationData":[TD([makeQuery(id+"F2.opExtrude","SWEPT_FACE",FACE,{"disambiguationData":[OSD([subQ0])]})])],"derivedFrom":makeQuery(id+"F3.boolean.opBoolean","COPY",FACE,{"derivedFrom":makeQuery(id+"F3.opExtrude","CAP_FACE",FACE,{"disambiguationData":[OSD([subQ0,subQ1,subQ2,subQ3,subQ4,subQ5,subQ6,subQ7])],"isStart":false})})}),makeQuery(id+"F8.opExtrude","SWEPT_FACE",FACE,{"disambiguationData":[OSD([sQuery(id+"F7.wireOp",EDGE,"E67")])]})]});}
            var Q5;
            Q5=makeQuery(id+"F8.boolean.opBoolean","INTERSECT",EDGE,{"disambiguationData":[OD(0.0)],"derivedFrom":[makeQuery(id+"F5.opExtrude","SWEPT_FACE",FACE,{"disambiguationData":[OSD([sQuery(id+"F4.wireOp",EDGE,"E30")])]}),makeQuery(id+"F8.opExtrude","SWEPT_FACE",FACE,{"disambiguationData":[OSD([sQuery(id+"F7.wireOp",EDGE,"E67")])]})]});
            fillet(context, id + "F14", {"entities" : qUnion([Q0, Q1, Q2, Q3, Q4, Q5]), "radius" : 3 * mm, "tangentPropagation" : true, "allowEdgeOverflow" : false});
        }
        {
            var Q0;
            Q0=makeQuery(id+"F1.opExtrude","CAP_EDGE",EDGE,{"disambiguationData":[OSD([sQuery(id+"F0.wireOp",EDGE,"E1.bottom")])],"isStart":false});
            fillet(context, id + "F15", {"entities" : qUnion([Q0]), "radius" : 2 * mm, "tangentPropagation" : true, "allowEdgeOverflow" : false});
        }
        {
            var Q0;
            {var subQ0=sQuery(id+"F0.wireOp",EDGE,"E22.filletArc");var subQ1=sQuery(id+"F0.wireOp",EDGE,"E7");var subQ2=sQuery(id+"F0.wireOp",EDGE,"E6");var subQ3=sQuery(id+"F0.wireOp",EDGE,"E5");var subQ4=sQuery(id+"F0.wireOp",EDGE,"E4");var subQ5=sQuery(id+"F0.wireOp",EDGE,"E1.bottom");var subQ6=sQuery(id+"F0.wireOp",EDGE,"E21.filletArc");var subQ7=sQuery(id+"F0.wireOp",EDGE,"E1.top");var subQ8=sQuery(id+"F0.wireOp",EDGE,"E1.left");var subQ9=sQuery(id+"F0.wireOp",EDGE,"E1.right");var subQ10=sQuery(id+"F0.wireOp",EDGE,"E23.filletArc");var subQ11=sQuery(id+"F0.wireOp",EDGE,"E24.filletArc");Q0=makeQuery(id+"F2.boolean.opBoolean","SPLIT",FACE,{"disambiguationData":[TD([makeQuery(id+"F1.opExtrude","SWEPT_FACE",FACE,{"disambiguationData":[OSD([subQ5])]})])],"derivedFrom":makeQuery(id+"F1.opExtrude","CAP_FACE",FACE,{"disambiguationData":[OSD([subQ5,subQ7,subQ8,subQ9,subQ4,subQ3,subQ2,subQ1,subQ6,subQ0,subQ10,subQ11])],"isStart":true})});}
            var sketch = newSketch(context, id + "F16", { "sketchPlane" : qUnion([Q0])});
            skLineSegment(sketch, "E79", {"start": v(0, 80) * mm, "end": v(0, 110) * mm, "construction": true});
            skCircle(sketch, "E80", {"center": v(0, 110) * mm, "radius": 6 * mm});
            skLineSegment(sketch, "E81", {"start": v(-33, 80) * mm, "end": v(-15, 98) * mm});
            skLineSegment(sketch, "E82", {"start": v(-15, 98) * mm, "end": v(-15, 110) * mm});
            skLineSegment(sketch, "E83", {"start": v(33, 80) * mm, "end": v(15, 98) * mm});
            skLineSegment(sketch, "E84", {"start": v(15, 98) * mm, "end": v(15, 110) * mm});
            skArc(sketch, "E85", {"start": v(15, 110) * mm, "mid": v(0, 125) * mm, "end": v(-15, 110) * mm});
            skLineSegment(sketch, "E86", {"start": v(-90, 0) * mm, "end": v(90, 0) * mm, "construction": true});
            skArc(sketch, "E87.MirrorCS", {"start": v(-15, 110) * mm, "mid": v(0, 125) * mm, "end": v(15, 110) * mm});
            skLineSegment(sketch, "E88.MirrorCS", {"start": v(90, 0) * mm, "end": v(-90, 0) * mm, "construction": true});
            skLineSegment(sketch, "E89.MirrorCS", {"start": v(33, -80) * mm, "end": v(15, -98) * mm});
            skLineSegment(sketch, "E90.MirrorCS", {"start": v(-33, -80) * mm, "end": v(-15, -98) * mm});
            skLineSegment(sketch, "E91.MirrorCS", {"start": v(15, -98) * mm, "end": v(15, -110) * mm});
            skLineSegment(sketch, "E92.MirrorCS", {"start": v(-15, -98) * mm, "end": v(-15, -110) * mm});
            skCircle(sketch, "E93.MirrorC", {"center": v(0, -110) * mm, "radius": 6 * mm});
            skArc(sketch, "E94.MirrorCS", {"start": v(15, -110) * mm, "mid": v(0, -125) * mm, "end": v(-15, -110) * mm});
            skLineSegment(sketch, "E95", {"start": v(0, -80) * mm, "end": v(0, -110) * mm, "construction": true});
            skSolve(sketch);
        }
        {
            var Q0;
            Q0=makeQuery(id+"F16.imprint","IMPRINT",FACE,{"disambiguationData":[TD([[makeQuery(id+"F16.imprint","IMPRINT",EDGE,{"derivedFrom":makeQuery(id+"F1.opExtrude","CAP_EDGE",EDGE,{"disambiguationData":[OSD([sQuery(id+"F0.wireOp",EDGE,"E1.left")])],"isStart":true})}),-1.0]])]});
            var Q1;
            Q1=makeQuery(id+"F16.imprint","IMPRINT",FACE,{"disambiguationData":[TD([[makeQuery(id+"F16.imprint","IMPRINT",EDGE,{"derivedFrom":sQuery(id+"F16.wireOp",EDGE,"E84")}),1.0]])]});
            var Q2;
            {var subQ0=sQuery(id+"F16.wireOp",EDGE,"E89.MirrorCS");Q2=makeQuery(id+"F16.imprint","IMPRINT",FACE,{"disambiguationData":[TD([[makeQuery(id+"F16.imprint","IMPRINT",EDGE,{"derivedFrom":subQ0}),-1.0]])]});}
            extrude(context, id + "F17", {"entities" : qUnion([Q0, Q1, Q2]), "operationType" : NewBodyOperationType.ADD, "endBound" : BoundingType.SYMMETRIC, "depth" : 6 * mm});
        }
    });
